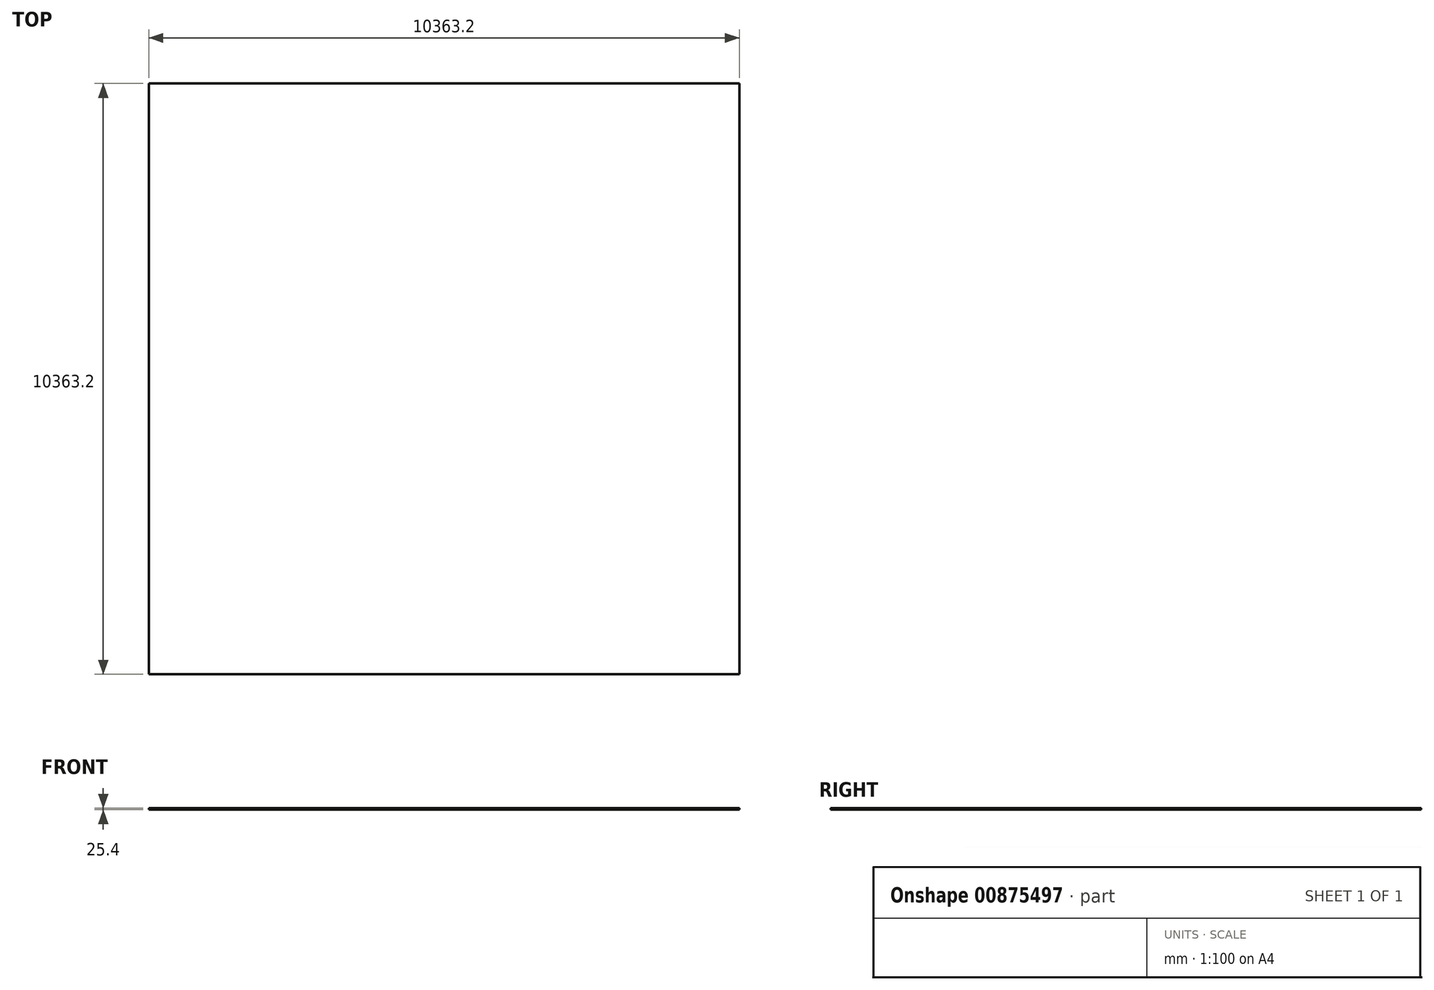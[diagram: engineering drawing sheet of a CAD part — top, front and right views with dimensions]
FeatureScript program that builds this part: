
annotation { "Feature Type Name" : "Feature", "Feature Type Description" : "" }
export const myFeature = defineFeature(function(context is Context, id is Id, definition is map)
    precondition{}
    {
        {
            var Q0;
            Q0=qCreatedBy(makeId("Top.planeOp"),FACE);
            var sketch = newSketch(context, id + "F0", { "sketchPlane" : qUnion([Q0])});
            skLineSegment(sketch, "E0.bottom", {"start": v(-4126.13, 7338) * mm, "end": v(6237.07, 7338) * mm});
            skLineSegment(sketch, "E0.top", {"start": v(-4126.13, -3025.2) * mm, "end": v(6237.07, -3025.2) * mm});
            skLineSegment(sketch, "E0.left", {"start": v(-4126.13, 7338) * mm, "end": v(-4126.13, -3025.2) * mm});
            skLineSegment(sketch, "E0.right", {"start": v(6237.07, 7338) * mm, "end": v(6237.07, -3025.2) * mm});
            skSolve(sketch);
        }
        {
            var Q0;
            Q0=makeQuery(id+"F0.imprint","IMPRINT",FACE,{"disambiguationData":[TD([[makeQuery(id+"F0.imprint","IMPRINT",EDGE,{"derivedFrom":sQuery(id+"F0.wireOp",EDGE,"E0.bottom")}),-1.0]])]});
            extrude(context, id + "F1", {"entities" : qUnion([Q0]), "depth" : 25.4 * mm, "offsetDistance" : 25.4 * mm});
        }
    });
